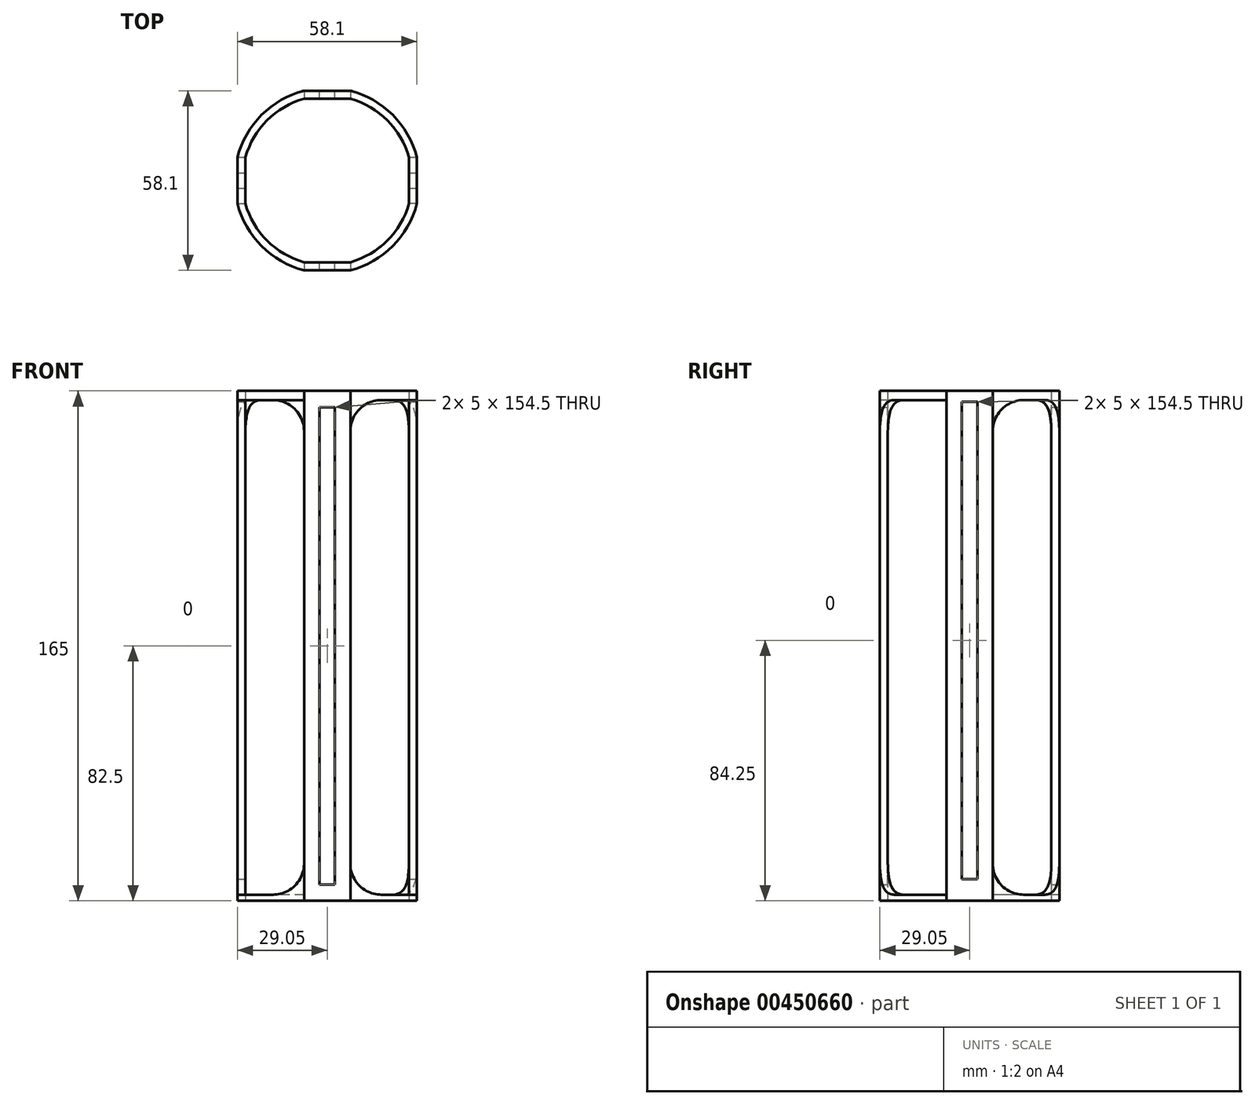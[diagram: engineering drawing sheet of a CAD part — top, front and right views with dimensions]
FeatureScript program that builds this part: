
annotation { "Feature Type Name" : "Feature", "Feature Type Description" : "" }
export const myFeature = defineFeature(function(context is Context, id is Id, definition is map)
    precondition{}
    {
        {
            var Q0;
            Q0=qCreatedBy(makeId("Top.planeOp"),FACE);
            var sketch = newSketch(context, id + "F0", { "sketchPlane" : qUnion([Q0])});
            skArc(sketch, "E0", {"start": v(-29.05, -7.5) * mm, "mid": v(-21.21, -21.21) * mm, "end": v(-7.5, -29.05) * mm});
            skArc(sketch, "E1", {"start": v(-26.46, -7.5) * mm, "mid": v(-19.45, -19.45) * mm, "end": v(-7.5, -26.46) * mm});
            skLineSegment(sketch, "E2", {"start": v(-26.46, 7.5) * mm, "end": v(-26.46, -7.5) * mm});
            skLineSegment(sketch, "E3", {"start": v(-29.05, 7.5) * mm, "end": v(-29.05, -7.5) * mm});
            skLineSegment(sketch, "E4.MirrorCS", {"start": v(26.46, 7.5) * mm, "end": v(26.46, -7.5) * mm});
            skLineSegment(sketch, "E5.MirrorCS", {"start": v(29.05, 7.5) * mm, "end": v(29.05, -7.5) * mm});
            skArc(sketch, "E6.trimOffspring", {"start": v(26.46, 7.5) * mm, "mid": v(19.45, 19.45) * mm, "end": v(7.5, 26.46) * mm});
            skArc(sketch, "E7.trimOffspring", {"start": v(29.05, 7.5) * mm, "mid": v(21.21, 21.21) * mm, "end": v(7.5, 29.05) * mm});
            skLineSegment(sketch, "E8", {"start": v(-7.5, -26.46) * mm, "end": v(7.5, -26.46) * mm});
            skLineSegment(sketch, "E9", {"start": v(-7.5, -29.05) * mm, "end": v(7.5, -29.05) * mm});
            skArc(sketch, "E10.trimOffspring", {"start": v(7.5, -26.46) * mm, "mid": v(19.45, -19.45) * mm, "end": v(26.46, -7.5) * mm});
            skArc(sketch, "E11.trimOffspring", {"start": v(7.5, -29.05) * mm, "mid": v(21.21, -21.21) * mm, "end": v(29.05, -7.5) * mm});
            skLineSegment(sketch, "E12.MirrorCS", {"start": v(-7.5, 26.46) * mm, "end": v(7.5, 26.46) * mm});
            skLineSegment(sketch, "E13.MirrorCS", {"start": v(-7.5, 29.05) * mm, "end": v(7.5, 29.05) * mm});
            skArc(sketch, "E14.trimOffspring", {"start": v(-7.5, 29.05) * mm, "mid": v(-21.21, 21.21) * mm, "end": v(-29.05, 7.5) * mm});
            skArc(sketch, "E15.trimOffspring", {"start": v(-7.5, 26.46) * mm, "mid": v(-19.45, 19.45) * mm, "end": v(-26.46, 7.5) * mm});
            skSolve(sketch);
        }
        {
            var Q0;
            Q0=makeQuery(id+"F0.imprint","IMPRINT",FACE,{"disambiguationData":[TD([[makeQuery(id+"F0.imprint","IMPRINT",EDGE,{"derivedFrom":sQuery(id+"F0.wireOp",EDGE,"E0")}),1.0]])]});
            extrude(context, id + "F1", {"entities" : qUnion([Q0]), "depth" : 2 * mm});
        }
        {
            var Q0;
            Q0=makeQuery(id+"F1.opExtrude","CAP_FACE",FACE,{"disambiguationData":[OSD([sQuery(id+"F0.wireOp",EDGE,"E0"),sQuery(id+"F0.wireOp",EDGE,"E1"),sQuery(id+"F0.wireOp",EDGE,"E2"),sQuery(id+"F0.wireOp",EDGE,"E3"),sQuery(id+"F0.wireOp",EDGE,"E4.MirrorCS"),sQuery(id+"F0.wireOp",EDGE,"E5.MirrorCS"),sQuery(id+"F0.wireOp",EDGE,"E6.trimOffspring"),sQuery(id+"F0.wireOp",EDGE,"E7.trimOffspring")])],"isStart":false});
            var sketch = newSketch(context, id + "F2", { "sketchPlane" : qUnion([Q0])});
            skLineSegment(sketch, "E16.bottom", {"start": v(-29.05, -7.5) * mm, "end": v(-26.46, -7.5) * mm});
            skLineSegment(sketch, "E16.top", {"start": v(-29.05, -7.5) * mm, "end": v(-26.46, -7.5) * mm});
            skLineSegment(sketch, "E16.left", {"start": v(-29.05, -7.5) * mm, "end": v(-29.05, -7.5) * mm});
            skLineSegment(sketch, "E16.right", {"start": v(-26.46, -7.5) * mm, "end": v(-26.46, -7.5) * mm});
            skLineSegment(sketch, "E17.MirrorCS", {"start": v(26.46, -7.5) * mm, "end": v(26.46, -7.5) * mm});
            skLineSegment(sketch, "E18.MirrorCS", {"start": v(29.05, -7.5) * mm, "end": v(29.05, -7.5) * mm});
            skLineSegment(sketch, "E19.MirrorCS", {"start": v(29.05, -7.5) * mm, "end": v(26.46, -7.5) * mm});
            skLineSegment(sketch, "E20.bottom", {"start": v(-7.5, -26.46) * mm, "end": v(7.5, -26.46) * mm});
            skLineSegment(sketch, "E20.top", {"start": v(-7.5, -29.05) * mm, "end": v(7.5, -29.05) * mm});
            skLineSegment(sketch, "E20.left", {"start": v(-7.5, -26.46) * mm, "end": v(-7.5, -29.05) * mm});
            skLineSegment(sketch, "E20.right", {"start": v(7.5, -26.46) * mm, "end": v(7.5, -29.05) * mm});
            skLineSegment(sketch, "E21.bottom", {"start": v(-7.5, 29.05) * mm, "end": v(7.5, 29.05) * mm});
            skLineSegment(sketch, "E21.top", {"start": v(-7.5, 26.46) * mm, "end": v(7.5, 26.46) * mm});
            skLineSegment(sketch, "E21.left", {"start": v(-7.5, 29.05) * mm, "end": v(-7.5, 26.46) * mm});
            skLineSegment(sketch, "E21.right", {"start": v(7.5, 29.05) * mm, "end": v(7.5, 26.46) * mm});
            skLineSegment(sketch, "E22.bottom", {"start": v(-29.05, 7.5) * mm, "end": v(-26.46, 7.5) * mm});
            skLineSegment(sketch, "E22.left", {"start": v(-29.05, 7.5) * mm, "end": v(-29.05, -7.5) * mm});
            skLineSegment(sketch, "E22.right", {"start": v(-26.46, 7.5) * mm, "end": v(-26.46, -7.5) * mm});
            skLineSegment(sketch, "E23.bottom", {"start": v(26.46, 7.5) * mm, "end": v(29.05, 7.5) * mm});
            skLineSegment(sketch, "E23.top", {"start": v(26.46, -7.5) * mm, "end": v(29.05, -7.5) * mm});
            skLineSegment(sketch, "E23.left", {"start": v(26.46, 7.5) * mm, "end": v(26.46, -7.5) * mm});
            skLineSegment(sketch, "E23.right", {"start": v(29.05, 7.5) * mm, "end": v(29.05, -7.5) * mm});
            skSolve(sketch);
        }
        {
            var Q0;
            Q0 = qSketchRegion(id + "F2", true);
            extrude(context, id + "F3", {"entities" : qUnion([Q0]), "operationType" : NewBodyOperationType.ADD, "depth" : 160 * mm});
        }
        {
            var Q0;
            Q0=makeQuery(id+"F3.opExtrude","CAP_EDGE",EDGE,{"disambiguationData":[OSD([sQuery(id+"F2.wireOp",EDGE,"E16.bottom")])],"isStart":true});
            var Q1;
            Q1=makeQuery(id+"F3.opExtrude","CAP_EDGE",EDGE,{"disambiguationData":[OSD([sQuery(id+"F2.wireOp",EDGE,"E20.left")])],"isStart":true});
            var Q2;
            Q2=makeQuery(id+"F3.opExtrude","CAP_EDGE",EDGE,{"disambiguationData":[OSD([sQuery(id+"F2.wireOp",EDGE,"E21.left")])],"isStart":true});
            var Q3;
            Q3=makeQuery(id+"F3.opExtrude","CAP_EDGE",EDGE,{"disambiguationData":[OSD([sQuery(id+"F2.wireOp",EDGE,"E22.bottom")])],"isStart":true});
            var Q4;
            Q4=makeQuery(id+"F3.opExtrude","CAP_EDGE",EDGE,{"disambiguationData":[OSD([sQuery(id+"F2.wireOp",EDGE,"E23.bottom")])],"isStart":true});
            var Q5;
            Q5=makeQuery(id+"F3.opExtrude","CAP_EDGE",EDGE,{"disambiguationData":[OSD([sQuery(id+"F2.wireOp",EDGE,"E21.right")])],"isStart":true});
            var Q6;
            Q6=makeQuery(id+"F3.opExtrude","CAP_EDGE",EDGE,{"disambiguationData":[OSD([sQuery(id+"F2.wireOp",EDGE,"E23.top")])],"isStart":true});
            var Q7;
            Q7=makeQuery(id+"F3.opExtrude","CAP_EDGE",EDGE,{"disambiguationData":[OSD([sQuery(id+"F2.wireOp",EDGE,"E20.right")])],"isStart":true});
            fillet(context, id + "F4", {"entities" : qUnion([Q0, Q1, Q2, Q3, Q4, Q5, Q6, Q7]), "radius" : 10 * mm, "tangentPropagation" : true, "allowEdgeOverflow" : false});
        }
        {
            var Q0;
            Q0=makeQuery(id+"F3.opExtrude","CAP_FACE",FACE,{"disambiguationData":[OSD([sQuery(id+"F2.wireOp",EDGE,"E23.bottom"),sQuery(id+"F2.wireOp",EDGE,"E23.top"),sQuery(id+"F2.wireOp",EDGE,"E23.left"),sQuery(id+"F2.wireOp",EDGE,"E23.right")])],"isStart":false});
            var sketch = newSketch(context, id + "F5", { "sketchPlane" : qUnion([Q0])});
            skArc(sketch, "E24", {"start": v(-29.05, -7.5) * mm, "mid": v(-21.21, -21.21) * mm, "end": v(-7.5, -29.05) * mm});
            skArc(sketch, "E25", {"start": v(-26.46, -7.5) * mm, "mid": v(-19.45, -19.45) * mm, "end": v(-7.5, -26.46) * mm});
            skLineSegment(sketch, "E26", {"start": v(-26.46, 7.5) * mm, "end": v(-26.46, -7.5) * mm});
            skLineSegment(sketch, "E27", {"start": v(-29.05, 7.5) * mm, "end": v(-29.05, -7.5) * mm});
            skLineSegment(sketch, "E28.MirrorCS", {"start": v(26.46, 7.5) * mm, "end": v(26.46, -7.5) * mm});
            skLineSegment(sketch, "E29.MirrorCS", {"start": v(29.05, 7.5) * mm, "end": v(29.05, -7.5) * mm});
            skArc(sketch, "E30.trimOffspring", {"start": v(26.46, 7.5) * mm, "mid": v(19.45, 19.45) * mm, "end": v(7.5, 26.46) * mm});
            skArc(sketch, "E31.trimOffspring", {"start": v(29.05, 7.5) * mm, "mid": v(21.21, 21.21) * mm, "end": v(7.5, 29.05) * mm});
            skLineSegment(sketch, "E32", {"start": v(-7.5, -26.46) * mm, "end": v(7.5, -26.46) * mm});
            skLineSegment(sketch, "E33", {"start": v(-7.5, -29.05) * mm, "end": v(7.5, -29.05) * mm});
            skArc(sketch, "E34.trimOffspring", {"start": v(7.5, -26.46) * mm, "mid": v(19.45, -19.45) * mm, "end": v(26.46, -7.5) * mm});
            skArc(sketch, "E35.trimOffspring", {"start": v(7.5, -29.05) * mm, "mid": v(21.21, -21.21) * mm, "end": v(29.05, -7.5) * mm});
            skLineSegment(sketch, "E36.MirrorCS", {"start": v(-7.5, 26.46) * mm, "end": v(7.5, 26.46) * mm});
            skLineSegment(sketch, "E37.MirrorCS", {"start": v(-7.5, 29.05) * mm, "end": v(7.5, 29.05) * mm});
            skArc(sketch, "E38.trimOffspring", {"start": v(-7.5, 29.05) * mm, "mid": v(-21.21, 21.21) * mm, "end": v(-29.05, 7.5) * mm});
            skArc(sketch, "E39.trimOffspring", {"start": v(-7.5, 26.46) * mm, "mid": v(-19.45, 19.45) * mm, "end": v(-26.46, 7.5) * mm});
            skSolve(sketch);
        }
        {
            var Q0;
            Q0 = qSketchRegion(id + "F5", true);
            extrude(context, id + "F6", {"entities" : qUnion([Q0]), "operationType" : NewBodyOperationType.ADD, "depth" : 3 * mm});
        }
        {
            var Q0;
            Q0=makeQuery(id+"F3.opExtrude","CAP_EDGE",EDGE,{"disambiguationData":[OSD([sQuery(id+"F2.wireOp",EDGE,"E23.bottom")])],"isStart":false});
            var Q1;
            Q1=makeQuery(id+"F3.opExtrude","CAP_EDGE",EDGE,{"disambiguationData":[OSD([sQuery(id+"F2.wireOp",EDGE,"E21.right")])],"isStart":false});
            var Q2;
            Q2=makeQuery(id+"F3.opExtrude","CAP_EDGE",EDGE,{"disambiguationData":[OSD([sQuery(id+"F2.wireOp",EDGE,"E20.right")])],"isStart":false});
            var Q3;
            Q3=makeQuery(id+"F3.opExtrude","CAP_EDGE",EDGE,{"disambiguationData":[OSD([sQuery(id+"F2.wireOp",EDGE,"E23.top")])],"isStart":false});
            var Q4;
            Q4=makeQuery(id+"F3.opExtrude","CAP_EDGE",EDGE,{"disambiguationData":[OSD([sQuery(id+"F2.wireOp",EDGE,"E16.bottom")])],"isStart":false});
            var Q5;
            Q5=makeQuery(id+"F3.opExtrude","CAP_EDGE",EDGE,{"disambiguationData":[OSD([sQuery(id+"F2.wireOp",EDGE,"E20.left")])],"isStart":false});
            var Q6;
            Q6=makeQuery(id+"F3.opExtrude","CAP_EDGE",EDGE,{"disambiguationData":[OSD([sQuery(id+"F2.wireOp",EDGE,"E22.bottom")])],"isStart":false});
            var Q7;
            Q7=makeQuery(id+"F3.opExtrude","CAP_EDGE",EDGE,{"disambiguationData":[OSD([sQuery(id+"F2.wireOp",EDGE,"E21.left")])],"isStart":false});
            fillet(context, id + "F7", {"entities" : qUnion([Q0, Q1, Q2, Q3, Q4, Q5, Q6, Q7]), "radius" : 10 * mm, "tangentPropagation" : true, "allowEdgeOverflow" : false});
        }
        {
            var Q0;
            Q0=makeQuery(id+"F6.boolean.opBoolean","MERGE",FACE,{"derivedFrom":[makeQuery(id+"F3.boolean.opBoolean","MERGE",FACE,{"derivedFrom":[makeQuery(id+"F1.opExtrude","SWEPT_FACE",FACE,{"disambiguationData":[OSD([sQuery(id+"F0.wireOp",EDGE,"E5.MirrorCS")])]}),makeQuery(id+"F3.opExtrude","SWEPT_FACE",FACE,{"disambiguationData":[OSD([sQuery(id+"F2.wireOp",EDGE,"E23.right")])]})]}),makeQuery(id+"F6.opExtrude","SWEPT_FACE",FACE,{"disambiguationData":[OSD([sQuery(id+"F5.wireOp",EDGE,"E29.MirrorCS")])]})]});
            var sketch = newSketch(context, id + "F8", { "sketchPlane" : qUnion([Q0])});
            skLineSegment(sketch, "E40.bottom", {"start": v(-2.5, 7) * mm, "end": v(2.5, 7) * mm});
            skLineSegment(sketch, "E40.top", {"start": v(-2.5, 161.5) * mm, "end": v(2.5, 161.5) * mm});
            skLineSegment(sketch, "E40.left", {"start": v(-2.5, 7) * mm, "end": v(-2.5, 161.5) * mm});
            skLineSegment(sketch, "E40.right", {"start": v(2.5, 7) * mm, "end": v(2.5, 161.5) * mm});
            skSolve(sketch);
        }
        {
            var Q0;
            Q0 = qSketchRegion(id + "F8", true);
            extrude(context, id + "F9", {"entities" : qUnion([Q0]), "operationType" : NewBodyOperationType.REMOVE, "oppositeDirection" : true, "depth" : 85.5 * mm});
        }
        {
            var Q0;
            Q0=makeQuery(id+"F6.boolean.opBoolean","MERGE",FACE,{"derivedFrom":[makeQuery(id+"F3.boolean.opBoolean","MERGE",FACE,{"derivedFrom":[makeQuery(id+"F1.opExtrude","SWEPT_FACE",FACE,{"disambiguationData":[OSD([sQuery(id+"F0.wireOp",EDGE,"E13.MirrorCS")])]}),makeQuery(id+"F3.opExtrude","SWEPT_FACE",FACE,{"disambiguationData":[OSD([sQuery(id+"F2.wireOp",EDGE,"E21.bottom")])]})]}),makeQuery(id+"F6.opExtrude","SWEPT_FACE",FACE,{"disambiguationData":[OSD([sQuery(id+"F5.wireOp",EDGE,"E37.MirrorCS")])]})]});
            var sketch = newSketch(context, id + "F10", { "sketchPlane" : qUnion([Q0])});
            skLineSegment(sketch, "E41.bottom", {"start": v(-2.5, 5.25) * mm, "end": v(2.5, 5.25) * mm});
            skLineSegment(sketch, "E41.top", {"start": v(-2.5, 159.75) * mm, "end": v(2.5, 159.75) * mm});
            skLineSegment(sketch, "E41.left", {"start": v(-2.5, 5.25) * mm, "end": v(-2.5, 159.75) * mm});
            skLineSegment(sketch, "E41.right", {"start": v(2.5, 5.25) * mm, "end": v(2.5, 159.75) * mm});
            skSolve(sketch);
        }
        {
            var Q0;
            Q0 = qSketchRegion(id + "F10", true);
            extrude(context, id + "F11", {"entities" : qUnion([Q0]), "operationType" : NewBodyOperationType.REMOVE, "oppositeDirection" : true, "depth" : 94.8 * mm});
        }
    });
